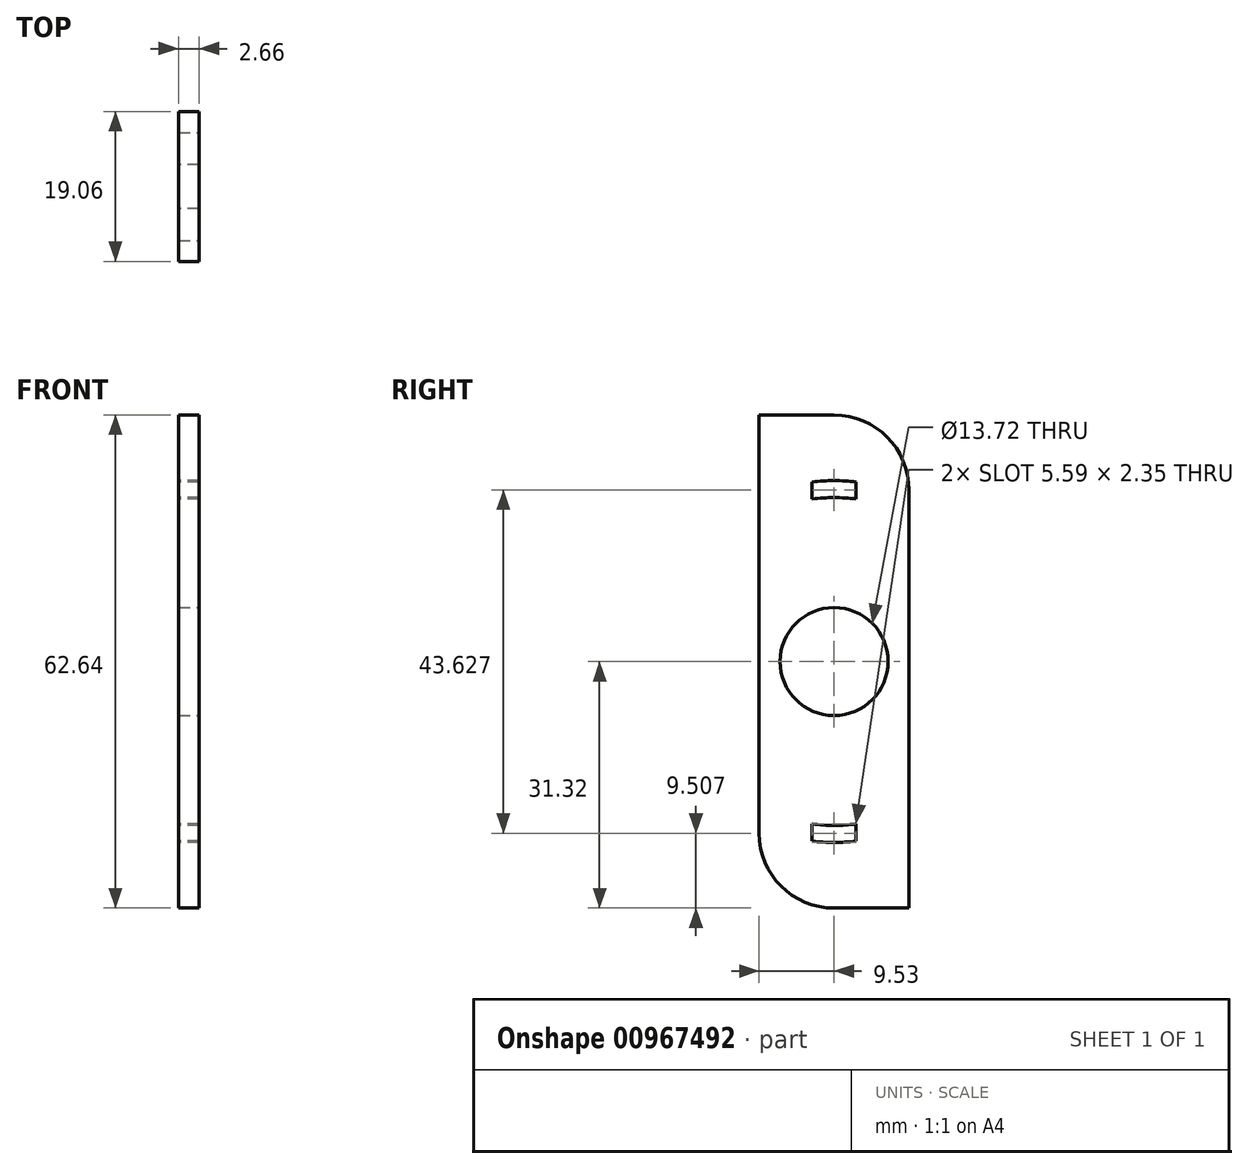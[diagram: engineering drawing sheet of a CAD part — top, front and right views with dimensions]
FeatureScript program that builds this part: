
annotation { "Feature Type Name" : "Feature", "Feature Type Description" : "" }
export const myFeature = defineFeature(function(context is Context, id is Id, definition is map)
    precondition{}
    {
        {
            var Q0;
            Q0=qCreatedBy(makeId("Right.planeOp"),FACE);
            var sketch = newSketch(context, id + "F0", { "sketchPlane" : qUnion([Q0])});
            skLineSegment(sketch, "E0", {"start": v(-54.35, 0) * mm, "end": v(51.75, 0) * mm, "construction": true});
            skLineSegment(sketch, "E1", {"start": v(0, 46.03) * mm, "end": v(0, -49.15) * mm, "construction": true});
            skLineSegment(sketch, "E2", {"start": v(-9.52, 31.32) * mm, "end": v(0, 31.32) * mm});
            skLineSegment(sketch, "E3", {"start": v(-9.52, 31.32) * mm, "end": v(-9.52, -21.8) * mm});
            skLineSegment(sketch, "E4", {"start": v(9.53, 21.8) * mm, "end": v(9.53, -31.32) * mm});
            skLineSegment(sketch, "E5", {"start": v(9.53, -31.32) * mm, "end": v(0, -31.32) * mm});
            skArc(sketch, "E6", {"start": v(-9.52, -21.8) * mm, "mid": v(-6.74, -28.53) * mm, "end": v(0, -31.32) * mm});
            skArc(sketch, "E7", {"start": v(9.53, 21.8) * mm, "mid": v(6.74, 28.53) * mm, "end": v(0, 31.32) * mm});
            skSolve(sketch);
        }
        {
            var Q0;
            Q0=makeQuery(id+"F0.imprint","IMPRINT",FACE,{"disambiguationData":[TD([[makeQuery(id+"F0.imprint","IMPRINT",EDGE,{"derivedFrom":sQuery(id+"F0.wireOp",EDGE,"E2")}),-1.0]])]});
            extrude(context, id + "F1", {"entities" : qUnion([Q0]), "endBound" : BoundingType.SYMMETRIC, "depth" : 2.66 * mm, "offsetDistance" : 25.4 * mm});
        }
        {
            var Q0;
            Q0=qCreatedBy(makeId("Right.planeOp"),FACE);
            var sketch = newSketch(context, id + "F2", { "sketchPlane" : qUnion([Q0])});
            skCircle(sketch, "E8", {"center": v(0, 0) * mm, "radius": 6.86 * mm});
            skSolve(sketch);
        }
        {
            var Q0;
            Q0 = qSketchRegion(id + "F2", true);
            extrude(context, id + "F3", {"entities" : qUnion([Q0]), "operationType" : NewBodyOperationType.REMOVE, "endBound" : BoundingType.THROUGH_ALL, "oppositeDirection" : true, "depth" : 25.4 * mm, "offsetDistance" : 25.4 * mm, "hasSecondDirection" : true, "secondDirectionBound" : SecondDirectionBoundingType.THROUGH_ALL, "secondDirectionOppositeDirection" : false, "secondDirectionDepth" : 25.4 * mm});
        }
        {
            var Q0;
            Q0=makeQuery(id+"F1.opExtrude","CAP_FACE",FACE,{"disambiguationData":[OSD([sQuery(id+"F0.wireOp",EDGE,"E2"),sQuery(id+"F0.wireOp",EDGE,"E3"),sQuery(id+"F0.wireOp",EDGE,"E4"),sQuery(id+"F0.wireOp",EDGE,"E5"),sQuery(id+"F0.wireOp",EDGE,"E6"),sQuery(id+"F0.wireOp",EDGE,"E7")])],"isStart":true});
            var sketch = newSketch(context, id + "F4", { "sketchPlane" : qUnion([Q0])});
            skArc(sketch, "E9", {"start": v(2.8, 22.82) * mm, "mid": v(0, 22.99) * mm, "end": v(-2.8, 22.82) * mm});
            skArc(sketch, "E10", {"start": v(2.8, 20.64) * mm, "mid": v(0, 20.83) * mm, "end": v(-2.8, 20.64) * mm});
            skLineSegment(sketch, "E11", {"start": v(-2.8, 22.82) * mm, "end": v(-2.8, 20.64) * mm});
            skLineSegment(sketch, "E12.MirrorCS", {"start": v(2.8, 22.82) * mm, "end": v(2.8, 20.64) * mm});
            skLineSegment(sketch, "E13.MirrorCS", {"start": v(-2.8, -22.82) * mm, "end": v(-2.8, -20.64) * mm});
            skArc(sketch, "E14.MirrorCS", {"start": v(2.8, -22.82) * mm, "mid": v(0, -22.99) * mm, "end": v(-2.8, -22.82) * mm});
            skLineSegment(sketch, "E15.MirrorCS", {"start": v(2.8, -22.82) * mm, "end": v(2.8, -20.64) * mm});
            skArc(sketch, "E16.MirrorCS", {"start": v(2.8, -20.64) * mm, "mid": v(0, -20.83) * mm, "end": v(-2.8, -20.64) * mm});
            skSolve(sketch);
        }
        {
            var Q0;
            Q0=makeQuery(id+"F4.imprint","IMPRINT",FACE,{"disambiguationData":[TD([[makeQuery(id+"F4.imprint","IMPRINT",EDGE,{"derivedFrom":sQuery(id+"F4.wireOp",EDGE,"E9")}),1.0]])]});
            var Q1;
            Q1=makeQuery(id+"F4.imprint","IMPRINT",FACE,{"disambiguationData":[TD([[makeQuery(id+"F4.imprint","IMPRINT",EDGE,{"derivedFrom":sQuery(id+"F4.wireOp",EDGE,"E13.MirrorCS")}),-1.0]])]});
            extrude(context, id + "F5", {"entities" : qUnion([Q0, Q1]), "operationType" : NewBodyOperationType.REMOVE, "endBound" : BoundingType.THROUGH_ALL, "oppositeDirection" : true, "depth" : 25.4 * mm, "offsetDistance" : 25.4 * mm});
        }
    });
